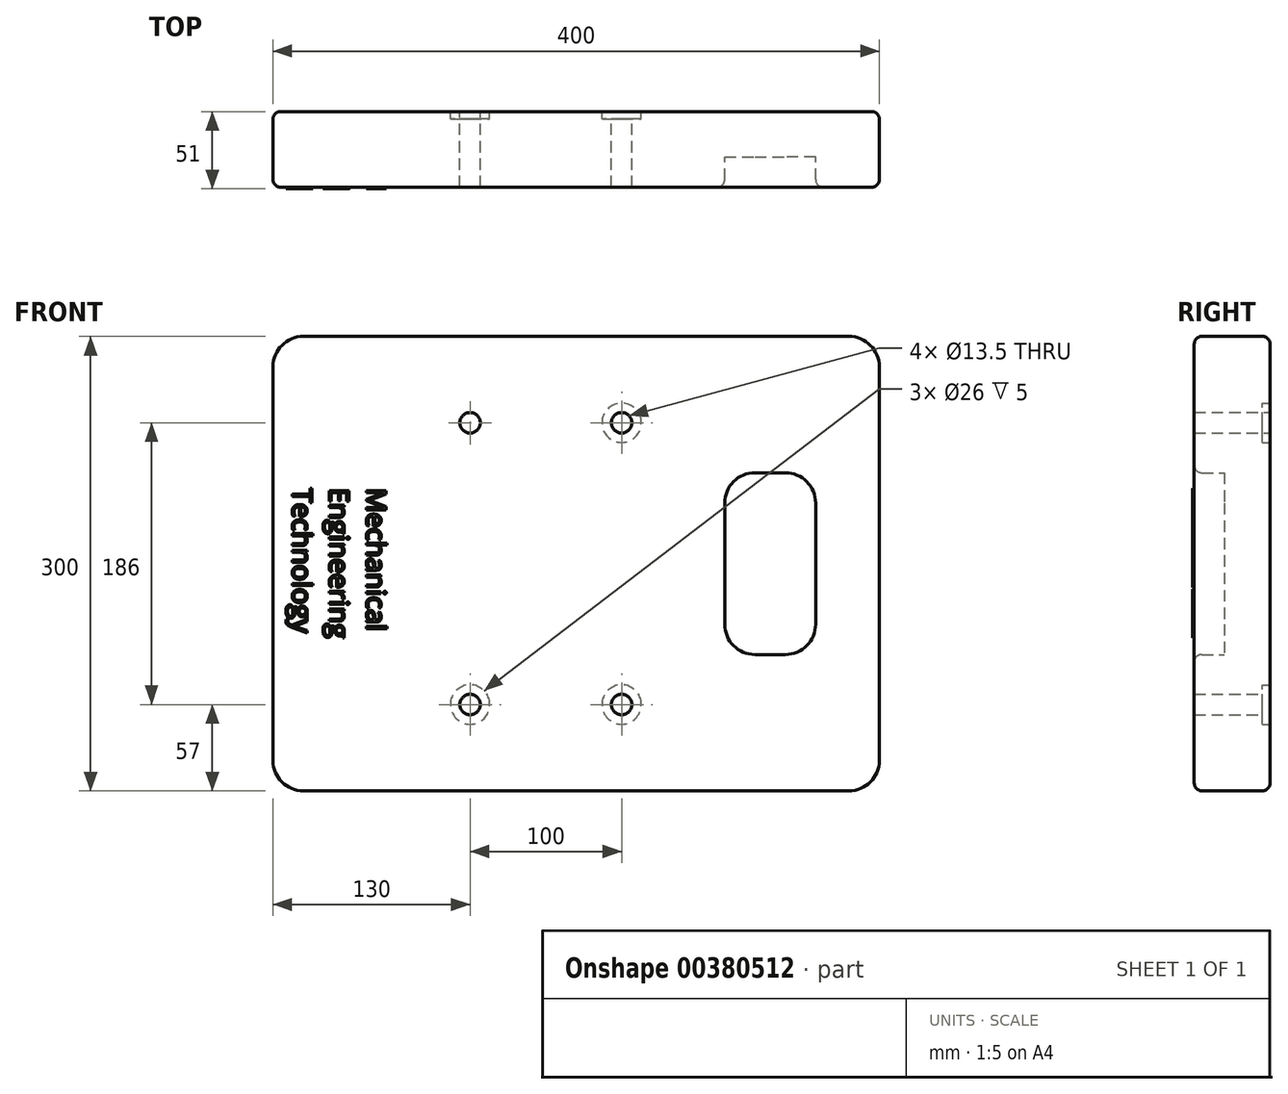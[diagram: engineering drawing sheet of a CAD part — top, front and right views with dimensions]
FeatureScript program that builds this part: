
annotation { "Feature Type Name" : "Feature", "Feature Type Description" : "" }
export const myFeature = defineFeature(function(context is Context, id is Id, definition is map)
    precondition{}
    {
        {
            var Q0;
            Q0=qCreatedBy(makeId("Front.planeOp"),FACE);
            var sketch = newSketch(context, id + "F0", { "sketchPlane" : qUnion([Q0])});
            skLineSegment(sketch, "E0.bottom", {"start": v(180, 150) * mm, "end": v(-180, 150) * mm});
            skLineSegment(sketch, "E0.top", {"start": v(180, -150) * mm, "end": v(-180, -150) * mm});
            skLineSegment(sketch, "E0.left", {"start": v(200, 130) * mm, "end": v(200, -130) * mm});
            skLineSegment(sketch, "E0.right", {"start": v(-200, 130) * mm, "end": v(-200, -130) * mm});
            skPoint(sketch, "E0.middle", {"position": v(0, 0) * mm});
            skPoint(sketch, "E1.startSnap0", {"position": v(-200, 0) * mm});
            skPoint(sketch, "E1.endSnap0", {"position": v(200, 0) * mm});
            skLineSegment(sketch, "E2", {"start": v(-200, 0) * mm, "end": v(158, 0) * mm, "construction": true});
            skLineSegment(sketch, "E3", {"start": v(158, 0) * mm, "end": v(158, 40) * mm});
            skLineSegment(sketch, "E4", {"start": v(158, 0) * mm, "end": v(158, -40) * mm});
            skLineSegment(sketch, "E5", {"start": v(138, 60) * mm, "end": v(118, 60) * mm});
            skLineSegment(sketch, "E6", {"start": v(98, 40) * mm, "end": v(98, -40) * mm});
            skLineSegment(sketch, "E7", {"start": v(118, -60) * mm, "end": v(138, -60) * mm});
            skPoint(sketch, "E8.visualSharp", {"position": v(-200, 150) * mm});
            skArc(sketch, "E8.filletArc", {"start": v(-180, 150) * mm, "mid": v(-194.14, 144.14) * mm, "end": v(-200, 130) * mm});
            skPoint(sketch, "E9.visualSharp", {"position": v(-200, -150) * mm});
            skArc(sketch, "E9.filletArc", {"start": v(-200, -130) * mm, "mid": v(-194.14, -144.14) * mm, "end": v(-180, -150) * mm});
            skPoint(sketch, "E10.visualSharp", {"position": v(200, -150) * mm});
            skArc(sketch, "E10.filletArc", {"start": v(180, -150) * mm, "mid": v(194.14, -144.14) * mm, "end": v(200, -130) * mm});
            skPoint(sketch, "E11.visualSharp", {"position": v(200, 150) * mm});
            skArc(sketch, "E11.filletArc", {"start": v(200, 130) * mm, "mid": v(194.14, 144.14) * mm, "end": v(180, 150) * mm});
            skPoint(sketch, "E12.visualSharp", {"position": v(98, 60) * mm});
            skArc(sketch, "E12.filletArc", {"start": v(118, 60) * mm, "mid": v(103.86, 54.14) * mm, "end": v(98, 40) * mm});
            skPoint(sketch, "E13.visualSharp", {"position": v(98, -60) * mm});
            skArc(sketch, "E13.filletArc", {"start": v(98, -40) * mm, "mid": v(103.86, -54.14) * mm, "end": v(118, -60) * mm});
            skPoint(sketch, "E14.visualSharp", {"position": v(158, -60) * mm});
            skArc(sketch, "E14.filletArc", {"start": v(138, -60) * mm, "mid": v(152.14, -54.14) * mm, "end": v(158, -40) * mm});
            skPoint(sketch, "E15.visualSharp", {"position": v(158, 60) * mm});
            skArc(sketch, "E15.filletArc", {"start": v(158, 40) * mm, "mid": v(152.14, 54.14) * mm, "end": v(138, 60) * mm});
            skLineSegment(sketch, "E16", {"start": v(200, -93) * mm, "end": v(30, -93) * mm, "construction": true});
            skCircle(sketch, "E17", {"center": v(30, -93) * mm, "radius": 6.75 * mm});
            skLineSegment(sketch, "E18", {"start": v(30, -93) * mm, "end": v(-70, -93) * mm, "construction": true});
            skCircle(sketch, "E19", {"center": v(-70, -93) * mm, "radius": 6.75 * mm});
            skCircle(sketch, "E20.MirrorC", {"center": v(-70, 93) * mm, "radius": 6.75 * mm});
            skCircle(sketch, "E21.MirrorC", {"center": v(30, 93) * mm, "radius": 6.75 * mm});
            skSolve(sketch);
        }
        {
            var Q0;
            Q0=makeQuery(id+"F0.imprint","IMPRINT",FACE,{"disambiguationData":[TD([[makeQuery(id+"F0.imprint","IMPRINT",EDGE,{"derivedFrom":sQuery(id+"F0.wireOp",EDGE,"E0.bottom")}),1.0]])]});
            extrude(context, id + "F1", {"entities" : qUnion([Q0]), "depth" : 50 * mm});
        }
        {
            var Q0;
            Q0=makeQuery(id+"F1.opExtrude","CAP_EDGE",EDGE,{"disambiguationData":[OSD([sQuery(id+"F0.wireOp",EDGE,"E0.left")])],"isStart":true});
            var Q1;
            Q1=makeQuery(id+"F1.opExtrude","CAP_EDGE",EDGE,{"disambiguationData":[OSD([sQuery(id+"F0.wireOp",EDGE,"E0.left")])],"isStart":false});
            var Q2;
            Q2=makeQuery(id+"F1.opExtrude","CAP_EDGE",EDGE,{"disambiguationData":[OSD([sQuery(id+"F0.wireOp",EDGE,"E3"),sQuery(id+"F0.wireOp",EDGE,"E4")])],"isStart":false});
            fillet(context, id + "F2", {"entities" : qUnion([Q0, Q1, Q2]), "radius" : 5 * mm, "tangentPropagation" : true, "allowEdgeOverflow" : false});
        }
        {
            var Q0;
            Q0=makeQuery(id+"F0.imprint","IMPRINT",FACE,{"disambiguationData":[TD([[makeQuery(id+"F0.imprint","IMPRINT",EDGE,{"derivedFrom":sQuery(id+"F0.wireOp",EDGE,"E3")}),1.0]])]});
            extrude(context, id + "F3", {"entities" : qUnion([Q0]), "operationType" : NewBodyOperationType.ADD, "depth" : 30 * mm});
        }
        {
            var Q0;
            Q0=makeQuery(id+"F0.imprint","IMPRINT",FACE,{"disambiguationData":[TD([[makeQuery(id+"F0.imprint","IMPRINT",EDGE,{"derivedFrom":sQuery(id+"F0.wireOp",EDGE,"E0.bottom")}),1.0]])]});
            var sketch = newSketch(context, id + "F4", { "sketchPlane" : qUnion([Q0])});
            skCircle(sketch, "E22.0", {"center": v(-70, 93) * mm, "radius": 6.75 * mm});
            skPoint(sketch, "E23.0", {"position": v(30, 93) * mm});
            skPoint(sketch, "E24.0", {"position": v(-70, -93) * mm});
            skLineSegment(sketch, "E25.0.0", {"start": v(-180, -150) * mm, "end": v(180, -150) * mm});
            skArc(sketch, "E25.0.1", {"start": v(180, -150) * mm, "mid": v(194.14, -144.14) * mm, "end": v(200, -130) * mm});
            skLineSegment(sketch, "E25.0.2", {"start": v(200, -130) * mm, "end": v(200, 130) * mm});
            skArc(sketch, "E25.0.3", {"start": v(200, 130) * mm, "mid": v(194.14, 144.14) * mm, "end": v(180, 150) * mm});
            skLineSegment(sketch, "E25.0.4", {"start": v(180, 150) * mm, "end": v(-180, 150) * mm});
            skArc(sketch, "E25.0.5", {"start": v(-180, 150) * mm, "mid": v(-194.14, 144.14) * mm, "end": v(-200, 130) * mm});
            skLineSegment(sketch, "E25.0.6", {"start": v(-200, 130) * mm, "end": v(-200, -130) * mm});
            skArc(sketch, "E25.0.7", {"start": v(-200, -130) * mm, "mid": v(-194.14, -144.14) * mm, "end": v(-180, -150) * mm});
            skCircle(sketch, "E26.0", {"center": v(30, -93) * mm, "radius": 6.75 * mm});
            skCircle(sketch, "E27.0", {"center": v(-70, -93) * mm, "radius": 6.75 * mm});
            skCircle(sketch, "E28", {"center": v(30, 93) * mm, "radius": 13 * mm});
            skCircle(sketch, "E29.MirrorC", {"center": v(30, -93) * mm, "radius": 13 * mm});
            skCircle(sketch, "E30", {"center": v(-70, 93) * mm, "radius": 13 * mm});
            skCircle(sketch, "E31", {"center": v(-70, -93) * mm, "radius": 13 * mm});
            skSolve(sketch);
        }
        {
            var Q0;
            Q0=makeQuery(id+"F4.imprint","IMPRINT",FACE,{"disambiguationData":[TD([[makeQuery(id+"F4.imprint","IMPRINT",EDGE,{"derivedFrom":sQuery(id+"F4.wireOp",EDGE,"E26.0")}),-1.0]])]});
            var Q1;
            Q1=makeQuery(id+"F4.imprint","IMPRINT",FACE,{"disambiguationData":[TD([[makeQuery(id+"F4.imprint","IMPRINT",EDGE,{"derivedFrom":sQuery(id+"F4.wireOp",EDGE,"E27.0")}),-1.0]])]});
            var Q2;
            Q2=makeQuery(id+"F4.imprint","IMPRINT",FACE,{"disambiguationData":[TD([[makeQuery(id+"F4.imprint","IMPRINT",EDGE,{"derivedFrom":sQuery(id+"F4.wireOp",EDGE,"E22.0")}),1.0]])]});
            var Q3;
            Q3=makeQuery(id+"F4.imprint","IMPRINT",FACE,{"disambiguationData":[TD([[makeQuery(id+"F4.imprint","IMPRINT",EDGE,{"derivedFrom":sQuery(id+"F4.wireOp",EDGE,"E28")}),1.0]])]});
            extrude(context, id + "F5", {"entities" : qUnion([Q0, Q1, Q2, Q3]), "operationType" : NewBodyOperationType.REMOVE, "depth" : 5 * mm});
        }
        {
            var Q0;
            Q0=makeQuery(id+"F1.opExtrude","CAP_FACE",FACE,{"disambiguationData":[OSD([sQuery(id+"F0.wireOp",EDGE,"E0.bottom"),sQuery(id+"F0.wireOp",EDGE,"E0.top"),sQuery(id+"F0.wireOp",EDGE,"E0.left"),sQuery(id+"F0.wireOp",EDGE,"E0.right"),sQuery(id+"F0.wireOp",EDGE,"E3"),sQuery(id+"F0.wireOp",EDGE,"E4"),sQuery(id+"F0.wireOp",EDGE,"E5"),sQuery(id+"F0.wireOp",EDGE,"E6"),sQuery(id+"F0.wireOp",EDGE,"E7"),sQuery(id+"F0.wireOp",EDGE,"E8.filletArc"),sQuery(id+"F0.wireOp",EDGE,"E9.filletArc"),sQuery(id+"F0.wireOp",EDGE,"E10.filletArc"),sQuery(id+"F0.wireOp",EDGE,"E11.filletArc"),sQuery(id+"F0.wireOp",EDGE,"E12.filletArc"),sQuery(id+"F0.wireOp",EDGE,"E13.filletArc"),sQuery(id+"F0.wireOp",EDGE,"E14.filletArc"),sQuery(id+"F0.wireOp",EDGE,"E15.filletArc"),sQuery(id+"F0.wireOp",EDGE,"E17"),sQuery(id+"F0.wireOp",EDGE,"E19"),sQuery(id+"F0.wireOp",EDGE,"E20.MirrorC"),sQuery(id+"F0.wireOp",EDGE,"E21.MirrorC")])],"isStart":false});
            var sketch = newSketch(context, id + "F6", { "sketchPlane" : qUnion([Q0])});
            skText(sketch, "E32", { "text": "Mechanical\nEngineering\nTechnology", "fontName": "OpenSans-Regular.ttf"});
            const initialGuessF6  = {"E32": [-0.13838, 0.05, 0, -1, 0.01293]};
            skSetInitialGuess(sketch, initialGuessF6);
            skSolve(sketch);
        }
        {
            var Q0;
            Q0=qSketchRegion(id+"F6",true);
            extrude(context, id + "F7", {"entities" : qUnion([Q0]), "operationType" : NewBodyOperationType.ADD, "depth" : 1 * mm});
        }
    });
